# Revit family: Valve_Box-Acudor-Recessed-ARVB_Series
name_source: partatom
category: Specialty Equipment
revit_build: Autodesk Revit 2014 (Build: 20130308_1515(x64)
units: mm (PartAtom-declared; Revit-internal decimal feet)

## types (6) — shared parameters
AKL - Allen Key Latch = No
Assembly Code = C1020700
CL - Cylinder Lock (one per door) = No
Default Elevation = 48"
Description = Recessed Valve Boxes
Door Gauge = No
Finish = Stainless Steel-Acudor-Type 304-Satin
Installation Type = Wall Mounted
MAS - Masonry Anchor Straps = No
Manufacturer = Acudor
Material = Stainless Steel-Acudor-Type 304-Satin
PC - Carbon steel with prime coat baked enamel finish = No
Product Documentation Link = https://www.acudor.com
Product Page URL = https://www.acudor.com
SC - stainless steel screwdriver operated cam latch = No
SS - Stainless Steel Construction (Type 304 No 4 Finish Satin Finish) = No
Screwdriver operated cam latch = No
Standard Latch = No
TH - 'T' Handle = No
URL = http://acudor.com
WC - knurled knob and flush key = No

## per-type parameters (varying)
| type | Height | Length | Width |
| ARVB 8x8x4 | 8" | 4" | 8" |
| ARVB 8x8x6 | 8" | 6" | 8" |
| ARVB 8x8x8 | 8" | 8" | 8" |
| ARVB 12x12x4 | 12" | 4" | 12" |
| ARVB 12x12x6 | 12" | 6" | 12" |
| ARVB 12x12x8 | 12" | 8" | 12" |

note: column(s) folded — value = type name in every type: Model

## geometry (parser evidence)
native form markers: Sweep x1
no freeform markers — native parametric forms only
